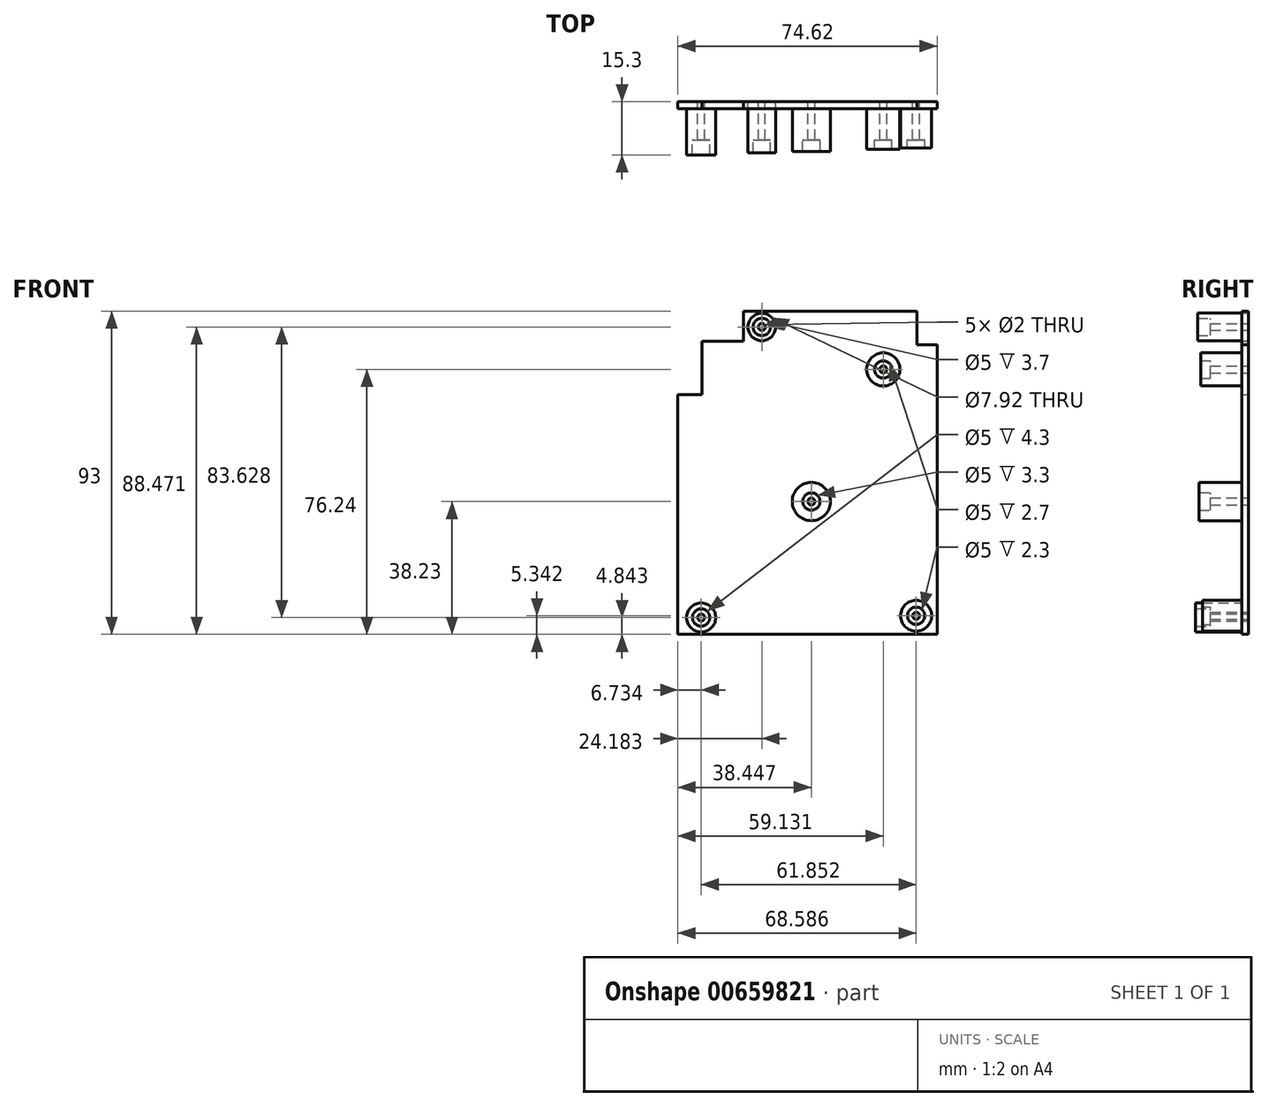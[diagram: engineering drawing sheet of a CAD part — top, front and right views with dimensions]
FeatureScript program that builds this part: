
annotation { "Feature Type Name" : "Feature", "Feature Type Description" : "" }
export const myFeature = defineFeature(function(context is Context, id is Id, definition is map)
    precondition{}
    {
        {
            var Q0;
            Q0=qCreatedBy(makeId("Front.planeOp"),FACE);
            var sketch = newSketch(context, id + "F0", { "sketchPlane" : qUnion([Q0])});
            skPoint(sketch, "E0.4.internal.snap0", {"position": v(-53.22, -38.23) * mm});
            skCircle(sketch, "E1", {"center": v(-20.76, -32.89) * mm, "radius": 4.45 * mm});
            skCircle(sketch, "E2", {"center": v(-50.9, 0) * mm, "radius": 5.5 * mm});
            skCircle(sketch, "E3", {"center": v(-30.22, 38.01) * mm, "radius": 4.77 * mm});
            skCircle(sketch, "E4", {"center": v(-82.62, -33.39) * mm, "radius": 4.19 * mm});
            skLineSegment(sketch, "E5", {"start": v(-66.63, 54.77) * mm, "end": v(-70.4, 54.77) * mm});
            skLineSegment(sketch, "E6", {"start": v(-70.4, 54.77) * mm, "end": v(-70.4, 46.07) * mm});
            skLineSegment(sketch, "E7", {"start": v(-82.36, 46.07) * mm, "end": v(-70.4, 46.07) * mm});
            skLineSegment(sketch, "E8", {"start": v(-82.36, 39.13) * mm, "end": v(-82.36, 46.07) * mm});
            skLineSegment(sketch, "E9", {"start": v(-89.35, 34.9) * mm, "end": v(-89.35, 34.9) * mm});
            skCircle(sketch, "E10", {"center": v(-65.17, 50.24) * mm, "radius": 3.96 * mm});
            skLineSegment(sketch, "E11", {"start": v(-20.55, 45.14) * mm, "end": v(-20.55, 54.77) * mm});
            skLineSegment(sketch, "E12", {"start": v(-14.73, 45.14) * mm, "end": v(-17.73, 45.14) * mm});
            skLineSegment(sketch, "E13", {"start": v(-82.36, 39.13) * mm, "end": v(-82.36, 30.79) * mm});
            skLineSegment(sketch, "E14", {"start": v(-82.36, 30.79) * mm, "end": v(-89.35, 30.79) * mm});
            skLineSegment(sketch, "E15", {"start": v(-66.63, 54.77) * mm, "end": v(-20.55, 54.77) * mm});
            skLineSegment(sketch, "E16", {"start": v(-20.55, 45.14) * mm, "end": v(-14.73, 45.14) * mm});
            skLineSegment(sketch, "E17", {"start": v(-14.73, -38.23) * mm, "end": v(-14.73, 45.14) * mm});
            skLineSegment(sketch, "E18", {"start": v(-89.35, 30.79) * mm, "end": v(-89.35, -38.23) * mm});
            skLineSegment(sketch, "E19", {"start": v(-89.35, -38.23) * mm, "end": v(-14.73, -38.23) * mm});
            skCircle(sketch, "E20", {"center": v(-65.17, 50.24) * mm, "radius": 1 * mm});
            skCircle(sketch, "E21", {"center": v(-30.22, 38.01) * mm, "radius": 1 * mm});
            skCircle(sketch, "E22", {"center": v(-50.9, 0) * mm, "radius": 1 * mm});
            skCircle(sketch, "E23", {"center": v(-82.62, -33.39) * mm, "radius": 1 * mm});
            skCircle(sketch, "E24", {"center": v(-20.76, -32.89) * mm, "radius": 1 * mm});
            skCircle(sketch, "E25", {"center": v(-82.62, -33.39) * mm, "radius": 2.5 * mm});
            skCircle(sketch, "E26", {"center": v(-20.76, -32.89) * mm, "radius": 2.5 * mm});
            skCircle(sketch, "E27", {"center": v(-50.9, 0) * mm, "radius": 2.5 * mm});
            skCircle(sketch, "E28", {"center": v(-65.17, 50.24) * mm, "radius": 2.5 * mm});
            skCircle(sketch, "E29", {"center": v(-30.22, 38.01) * mm, "radius": 2.5 * mm});
            skSolve(sketch);
        }
        {
            var Q0;
            Q0=makeQuery(id+"F0.imprint","IMPRINT",FACE,{"disambiguationData":[TD([[makeQuery(id+"F0.imprint","IMPRINT",EDGE,{"derivedFrom":sQuery(id+"F0.wireOp",EDGE,"E2")}),-1.0]])]});
            var Q1;
            Q1=makeQuery(id+"F0.imprint","IMPRINT",FACE,{"disambiguationData":[TD([[makeQuery(id+"F0.imprint","IMPRINT",EDGE,{"derivedFrom":sQuery(id+"F0.wireOp",EDGE,"E1")}),-1.0]])]});
            var Q2;
            {var subQ1=sQuery(id+"F0.wireOp",EDGE,"hO0eItjr-kAU9-zc48-p12e-SZQD80vzSGh9");Q2=makeQuery(id+"F0.imprint","IMPRINT",FACE,{"disambiguationData":[TD([[makeQuery(id+"F0.imprint","IMPRINT",EDGE,{"derivedFrom":subQ1}),-1.0]])]});}
            var Q3;
            {var subQ0=sQuery(id+"F0.wireOp",EDGE,"royT5C06-eYii-4xQR-Nwoi-XYeKaWnAis2P");Q3=makeQuery(id+"F0.imprint","IMPRINT",FACE,{"disambiguationData":[TD([[makeQuery(id+"F0.imprint","IMPRINT",EDGE,{"derivedFrom":subQ0}),1.0]])]});}
            extrude(context, id + "F1", {"entities" : qUnion([Q0, Q1, Q2, Q3]), "depth" : 2 * mm, "offsetDistance" : 25 * mm});
        }
        {
            var Q0;
            Q0=makeQuery(id+"F0.imprint","IMPRINT",FACE,{"disambiguationData":[TD([[makeQuery(id+"F0.imprint","IMPRINT",EDGE,{"derivedFrom":sQuery(id+"F0.wireOp",EDGE,"E4")}),-1.0]])]});
            extrude(context, id + "F2", {"entities" : qUnion([Q0]), "depth" : 2 * mm, "offsetDistance" : 25 * mm});
        }
        {
            var Q0;
            {var subQ4=sQuery(id+"F0.wireOp",EDGE,"E14");Q0=makeQuery(id+"F0.imprint","IMPRINT",FACE,{"disambiguationData":[TD([[makeQuery(id+"F0.imprint","IMPRINT",EDGE,{"derivedFrom":subQ4}),1.0]])]});}
            extrude(context, id + "F3", {"entities" : qUnion([Q0]), "depth" : 2 * mm, "offsetDistance" : 25 * mm});
        }
        {
            var Q0;
            Q0=makeQuery(id+"F0.imprint","IMPRINT",FACE,{"disambiguationData":[TD([[makeQuery(id+"F0.imprint","IMPRINT",EDGE,{"derivedFrom":sQuery(id+"F0.wireOp",EDGE,"E4")}),1.0]])]});
            extrude(context, id + "F4", {"entities" : qUnion([Q0]), "operationType" : NewBodyOperationType.ADD, "depth" : 15.3 * mm, "offsetDistance" : 25 * mm});
        }
        {
            var Q0;
            Q0=makeQuery(id+"F0.imprint","IMPRINT",FACE,{"disambiguationData":[TD([[makeQuery(id+"F0.imprint","IMPRINT",EDGE,{"derivedFrom":sQuery(id+"F0.wireOp",EDGE,"E2")}),1.0]])]});
            extrude(context, id + "F5", {"entities" : qUnion([Q0]), "operationType" : NewBodyOperationType.ADD, "depth" : 14.3 * mm, "offsetDistance" : 25 * mm});
        }
        {
            var Q0;
            Q0=makeQuery(id+"F0.imprint","IMPRINT",FACE,{"disambiguationData":[TD([[makeQuery(id+"F0.imprint","IMPRINT",EDGE,{"derivedFrom":sQuery(id+"F0.wireOp",EDGE,"E3")}),1.0]])]});
            extrude(context, id + "F6", {"entities" : qUnion([Q0]), "operationType" : NewBodyOperationType.ADD, "depth" : 13.7 * mm, "offsetDistance" : 25 * mm});
        }
        {
            var Q0;
            Q0=makeQuery(id+"F0.imprint","IMPRINT",FACE,{"disambiguationData":[TD([[makeQuery(id+"F0.imprint","IMPRINT",EDGE,{"derivedFrom":sQuery(id+"F0.wireOp",EDGE,"E1")}),1.0]])]});
            extrude(context, id + "F7", {"entities" : qUnion([Q0]), "operationType" : NewBodyOperationType.ADD, "depth" : 13.3 * mm, "offsetDistance" : 25 * mm});
        }
        {
            var Q0;
            Q0=makeQuery(id+"F0.imprint","IMPRINT",FACE,{"disambiguationData":[TD([[makeQuery(id+"F0.imprint","IMPRINT",EDGE,{"derivedFrom":sQuery(id+"F0.wireOp",EDGE,"E10")}),1.0]])]});
            extrude(context, id + "F8", {"entities" : qUnion([Q0]), "depth" : 14.7 * mm, "offsetDistance" : 25 * mm});
        }
        {
            var Q0;
            Q0=makeQuery(id+"F0.imprint","IMPRINT",FACE,{"disambiguationData":[TD([[makeQuery(id+"F0.imprint","IMPRINT",EDGE,{"derivedFrom":sQuery(id+"F0.wireOp",EDGE,"E20")}),1.0]])]});
            var Q1;
            Q1=makeQuery(id+"F0.imprint","IMPRINT",FACE,{"disambiguationData":[TD([[makeQuery(id+"F0.imprint","IMPRINT",EDGE,{"derivedFrom":sQuery(id+"F0.wireOp",EDGE,"wGUqUpFA-rsRI-hoJ0-mmaN-9bsGZRcwuFqq")}),1.0]])]});
            var Q2;
            Q2=makeQuery(id+"F0.imprint","IMPRINT",FACE,{"disambiguationData":[TD([[makeQuery(id+"F0.imprint","IMPRINT",EDGE,{"derivedFrom":sQuery(id+"F0.wireOp",EDGE,"E21")}),1.0]])]});
            var Q3;
            Q3=makeQuery(id+"F0.imprint","IMPRINT",FACE,{"disambiguationData":[TD([[makeQuery(id+"F0.imprint","IMPRINT",EDGE,{"derivedFrom":sQuery(id+"F0.wireOp",EDGE,"E23")}),1.0]])]});
            var Q4;
            Q4=makeQuery(id+"F0.imprint","IMPRINT",FACE,{"disambiguationData":[TD([[makeQuery(id+"F0.imprint","IMPRINT",EDGE,{"derivedFrom":sQuery(id+"F0.wireOp",EDGE,"E24")}),1.0]])]});
            var Q5;
            Q5=makeQuery(id+"F0.imprint","IMPRINT",FACE,{"disambiguationData":[TD([[makeQuery(id+"F0.imprint","IMPRINT",EDGE,{"derivedFrom":sQuery(id+"F0.wireOp",EDGE,"E22")}),1.0]])]});
            extrude(context, id + "F9", {"entities" : qUnion([Q0, Q1, Q2, Q3, Q4, Q5]), "operationType" : NewBodyOperationType.REMOVE, "depth" : 15 * mm, "offsetDistance" : 25 * mm});
        }
        {
            var Q0;
            Q0=makeQuery(id+"F0.imprint","IMPRINT",FACE,{"disambiguationData":[TD([[makeQuery(id+"F0.imprint","IMPRINT",EDGE,{"derivedFrom":sQuery(id+"F0.wireOp",EDGE,"E23")}),-1.0]])]});
            var Q1;
            Q1=makeQuery(id+"F0.imprint","IMPRINT",FACE,{"disambiguationData":[TD([[makeQuery(id+"F0.imprint","IMPRINT",EDGE,{"derivedFrom":sQuery(id+"F0.wireOp",EDGE,"E24")}),-1.0]])]});
            var Q2;
            Q2=makeQuery(id+"F0.imprint","IMPRINT",FACE,{"disambiguationData":[TD([[makeQuery(id+"F0.imprint","IMPRINT",EDGE,{"derivedFrom":sQuery(id+"F0.wireOp",EDGE,"E22")}),-1.0]])]});
            var Q3;
            Q3=makeQuery(id+"F0.imprint","IMPRINT",FACE,{"disambiguationData":[TD([[makeQuery(id+"F0.imprint","IMPRINT",EDGE,{"derivedFrom":sQuery(id+"F0.wireOp",EDGE,"wGUqUpFA-rsRI-hoJ0-mmaN-9bsGZRcwuFqq")}),-1.0]])]});
            var Q4;
            Q4=makeQuery(id+"F0.imprint","IMPRINT",FACE,{"disambiguationData":[TD([[makeQuery(id+"F0.imprint","IMPRINT",EDGE,{"derivedFrom":sQuery(id+"F0.wireOp",EDGE,"E20")}),-1.0]])]});
            var Q5;
            Q5=makeQuery(id+"F0.imprint","IMPRINT",FACE,{"disambiguationData":[TD([[makeQuery(id+"F0.imprint","IMPRINT",EDGE,{"derivedFrom":sQuery(id+"F0.wireOp",EDGE,"E21")}),-1.0]])]});
            extrude(context, id + "F10", {"entities" : qUnion([Q0, Q1, Q2, Q3, Q4, Q5]), "operationType" : NewBodyOperationType.ADD, "depth" : 11 * mm, "offsetDistance" : 25 * mm});
        }
    });
